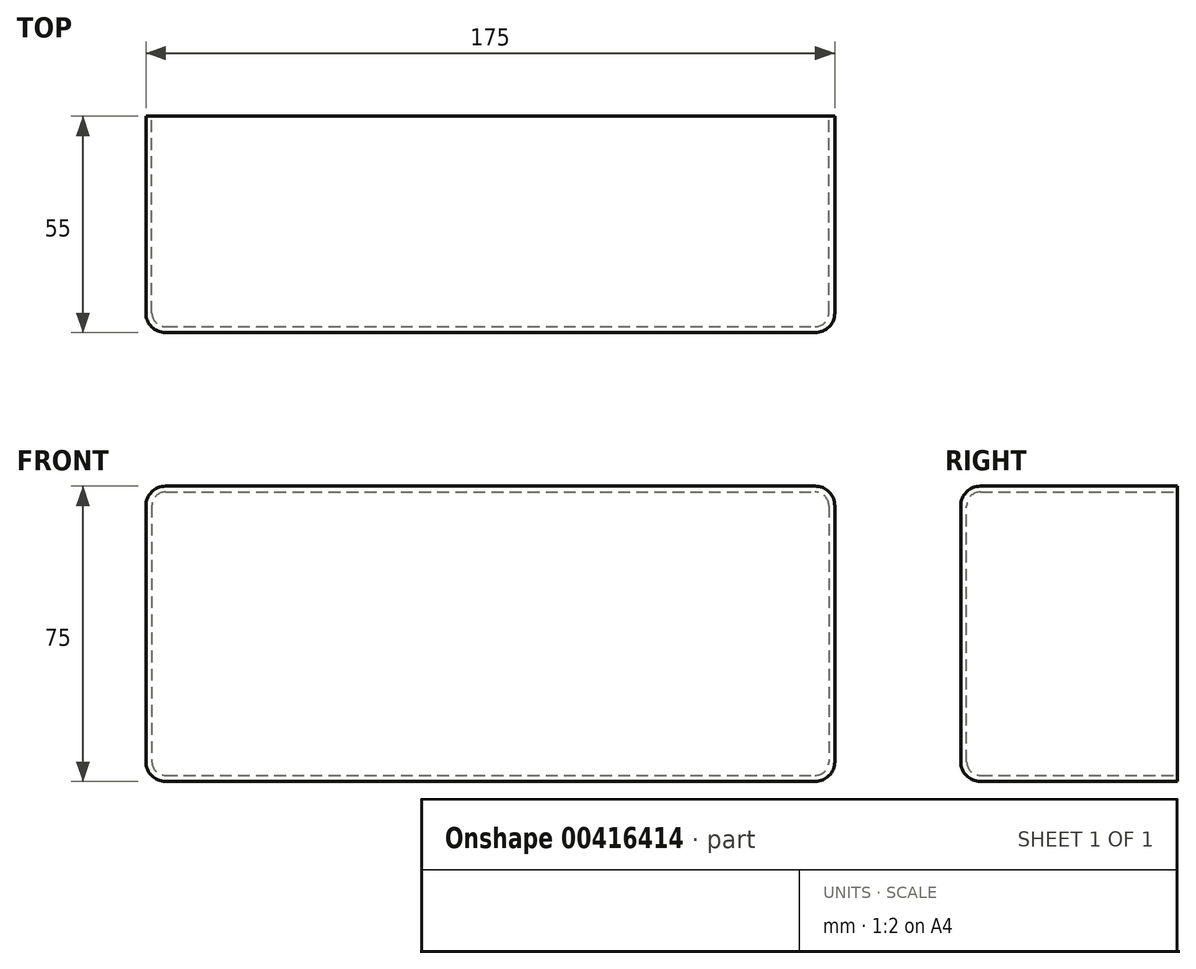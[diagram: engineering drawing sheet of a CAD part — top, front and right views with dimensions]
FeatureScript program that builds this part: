
annotation { "Feature Type Name" : "Feature", "Feature Type Description" : "" }
export const myFeature = defineFeature(function(context is Context, id is Id, definition is map)
    precondition{}
    {
        {
            var Q0;
            Q0=qCreatedBy(makeId("Front.planeOp"),FACE);
            var sketch = newSketch(context, id + "F0", { "sketchPlane" : qUnion([Q0])});
            skLineSegment(sketch, "E0.bottom", {"start": v(-55, 42.5) * mm, "end": v(120, 42.5) * mm});
            skLineSegment(sketch, "E0.top", {"start": v(-55, -32.5) * mm, "end": v(120, -32.5) * mm});
            skLineSegment(sketch, "E0.left", {"start": v(-55, 42.5) * mm, "end": v(-55, -32.5) * mm});
            skLineSegment(sketch, "E0.right", {"start": v(120, 42.5) * mm, "end": v(120, -32.5) * mm});
            skSolve(sketch);
        }
        {
            var Q0;
            Q0 = qSketchRegion(id + "F0", true);
            extrude(context, id + "F1", {"entities" : qUnion([Q0]), "flatOperationType" : FlatOperationType.REMOVE, "offsetDistance" : 25 * mm, "depth" : 55 * mm, "domain" : OperationDomain.MODEL});
        }
        {
            var Q0;
            Q0=makeQuery(id+"F1.opExtrude","CAP_EDGE",EDGE,{"disambiguationData":[OSD([sQuery(id+"F0.wireOp",EDGE,"E0.left")])],"isStart":false});
            var Q1;
            Q1=makeQuery(id+"F1.opExtrude","CAP_EDGE",EDGE,{"disambiguationData":[OSD([sQuery(id+"F0.wireOp",EDGE,"E0.bottom")])],"isStart":false});
            var Q2;
            Q2=makeQuery(id+"F1.opExtrude","CAP_EDGE",EDGE,{"disambiguationData":[OSD([sQuery(id+"F0.wireOp",EDGE,"E0.right")])],"isStart":false});
            var Q3;
            Q3=makeQuery(id+"F1.opExtrude","CAP_EDGE",EDGE,{"disambiguationData":[OSD([sQuery(id+"F0.wireOp",EDGE,"E0.top")])],"isStart":false});
            var Q4;
            Q4=makeQuery(id+"F1.opExtrude","SWEPT_EDGE",EDGE,{"disambiguationData":[OSD([sQuery(id+"F0.wireOp",EDGE,"E0.bottom"),sQuery(id+"F0.wireOp",EDGE,"E0.left")])]});
            var Q5;
            Q5=makeQuery(id+"F1.opExtrude","SWEPT_EDGE",EDGE,{"disambiguationData":[OSD([sQuery(id+"F0.wireOp",EDGE,"E0.bottom"),sQuery(id+"F0.wireOp",EDGE,"E0.right")])]});
            var Q6;
            Q6=makeQuery(id+"F1.opExtrude","SWEPT_EDGE",EDGE,{"disambiguationData":[OSD([sQuery(id+"F0.wireOp",EDGE,"E0.top"),sQuery(id+"F0.wireOp",EDGE,"E0.left")])]});
            var Q7;
            Q7=makeQuery(id+"F1.opExtrude","SWEPT_EDGE",EDGE,{"disambiguationData":[OSD([sQuery(id+"F0.wireOp",EDGE,"E0.top"),sQuery(id+"F0.wireOp",EDGE,"E0.right")])]});
            fillet(context, id + "F2", {"entities" : qUnion([Q0, Q1, Q2, Q3, Q4, Q5, Q6, Q7]), "radius" : 5 * mm, "tangentPropagation" : true, "allowEdgeOverflow" : false});
        }
        {
            var Q0;
            Q0=makeQuery(id+"F1.opExtrude","CAP_FACE",FACE,{"disambiguationData":[OSD([sQuery(id+"F0.wireOp",EDGE,"E0.bottom"),sQuery(id+"F0.wireOp",EDGE,"E0.top"),sQuery(id+"F0.wireOp",EDGE,"E0.left"),sQuery(id+"F0.wireOp",EDGE,"E0.right")])],"isStart":true});
            shell(context, id + "F3", {"entities" : qUnion([Q0]), "thickness" : 1.5 * mm});
        }
    });
